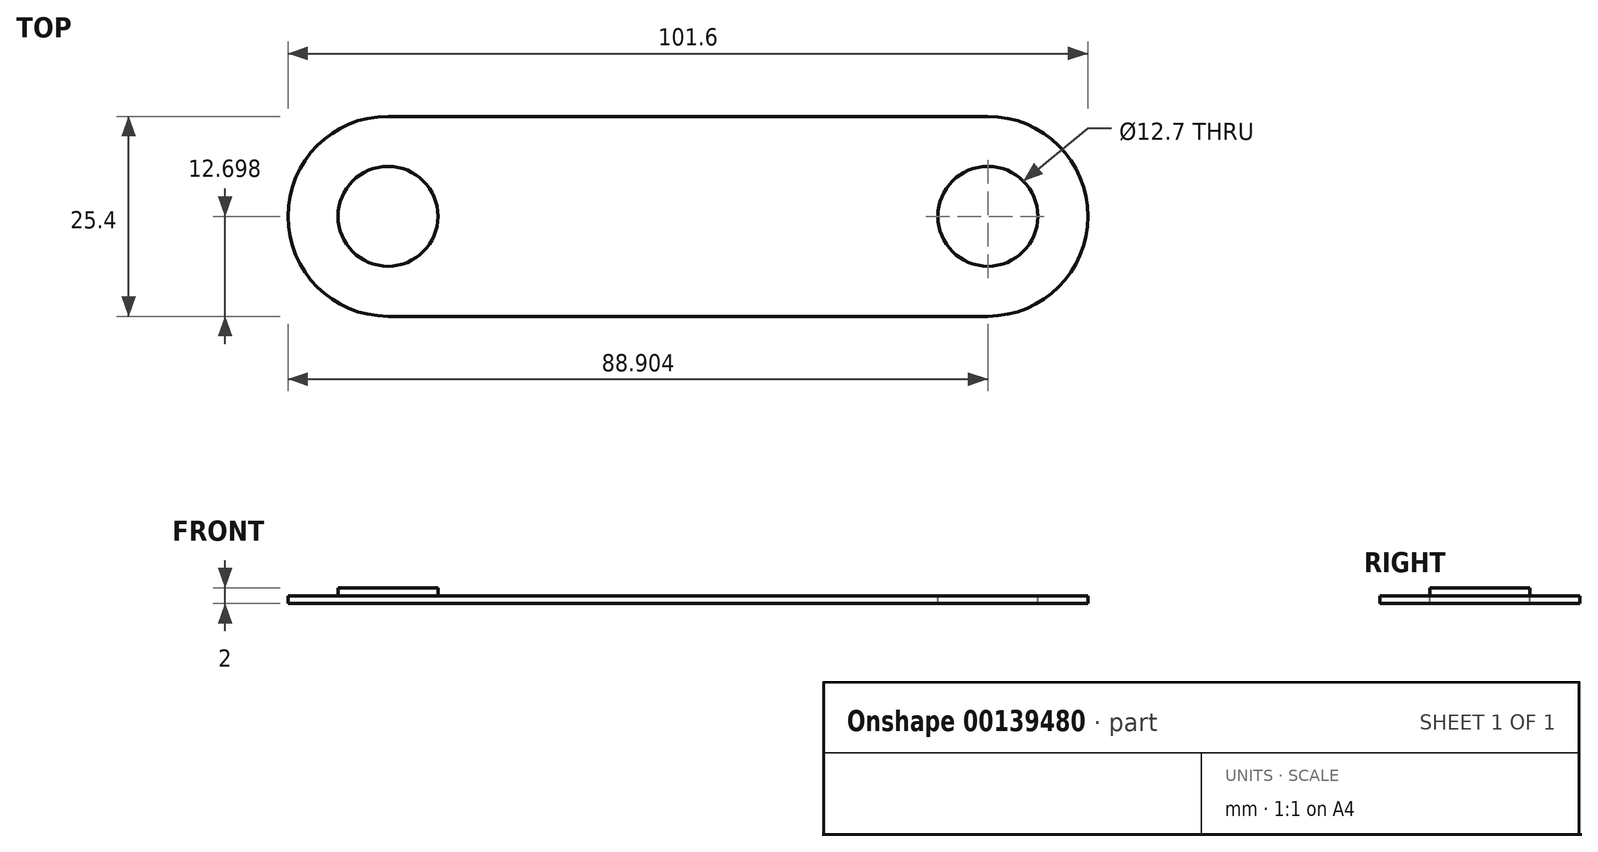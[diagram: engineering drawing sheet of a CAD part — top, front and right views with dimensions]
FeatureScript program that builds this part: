
annotation { "Feature Type Name" : "Feature", "Feature Type Description" : "" }
export const myFeature = defineFeature(function(context is Context, id is Id, definition is map)
    precondition{}
    {
        {
            assignVariable(context, id + "F0", {"name" : "depth", "anyValue" : 1});
        }
        {
            var Q0;
            Q0=qCreatedBy(makeId("Top.planeOp"),FACE);
            var sketch = newSketch(context, id + "F1", { "sketchPlane" : qUnion([Q0])});
            skLineSegment(sketch, "E0.bottom", {"start": v(-23.17, 15.12) * mm, "end": v(-99.37, 15.12) * mm});
            skLineSegment(sketch, "E0.top", {"start": v(-23.17, -10.28) * mm, "end": v(-99.37, -10.28) * mm});
            skPoint(sketch, "E0.middle", {"position": v(-61.27, 2.42) * mm});
            skArc(sketch, "E1", {"start": v(-99.37, 15.12) * mm, "mid": v(-112.07, 2.42) * mm, "end": v(-99.37, -10.28) * mm});
            skArc(sketch, "E2", {"start": v(-23.17, -10.28) * mm, "mid": v(-10.47, 2.42) * mm, "end": v(-23.17, 15.12) * mm});
            skSolve(sketch);
        }
        {
            var Q0;
            Q0 = qSketchRegion(id + "F1", true);
            extrude(context, id + "F2", {"entities" : qUnion([Q0]), "depth" : (getVariable(context, 'depth')) * mm});
        }
        {
            var Q0;
            Q0=makeQuery(id+"F2.opExtrude","CAP_FACE",FACE,{"disambiguationData":[OSD([sQuery(id+"F1.wireOp",EDGE,"E0.bottom"),sQuery(id+"F1.wireOp",EDGE,"E0.top"),sQuery(id+"F1.wireOp",EDGE,"E1"),sQuery(id+"F1.wireOp",EDGE,"E2")])],"isStart":false});
            var sketch = newSketch(context, id + "F3", { "sketchPlane" : qUnion([Q0])});
            skCircle(sketch, "E3", {"center": v(-99.37, 2.42) * mm, "radius": 6.35 * mm});
            skCircle(sketch, "E4", {"center": v(-23.17, 2.42) * mm, "radius": 6.35 * mm});
            skSolve(sketch);
        }
        {
            var Q0;
            Q0=makeQuery(id+"F3.imprint","IMPRINT",FACE,{"disambiguationData":[TD([[makeQuery(id+"F3.imprint","IMPRINT",EDGE,{"derivedFrom":sQuery(id+"F3.wireOp",EDGE,"E3")}),1.0]])]});
            var Q1;
            Q1=sQuery(id+"F3.wireOp",EDGE,"E3");
            extrude(context, id + "F4", {"entities" : qUnion([Q0]), "operationType" : NewBodyOperationType.ADD, "surfaceEntities" : qUnion([Q1]), "depth" : (getVariable(context, 'depth')) * mm});
        }
        {
            var Q0;
            Q0=makeQuery(id+"F3.imprint","IMPRINT",FACE,{"disambiguationData":[TD([[makeQuery(id+"F3.imprint","IMPRINT",EDGE,{"derivedFrom":sQuery(id+"F3.wireOp",EDGE,"E4")}),1.0]])]});
            var Q1;
            Q1=sQuery(id+"F3.wireOp",EDGE,"E4");
            extrude(context, id + "F5", {"entities" : qUnion([Q0]), "operationType" : NewBodyOperationType.REMOVE, "surfaceEntities" : qUnion([Q1]), "oppositeDirection" : true, "depth" : (getVariable(context, 'depth')) * mm});
        }
    });
